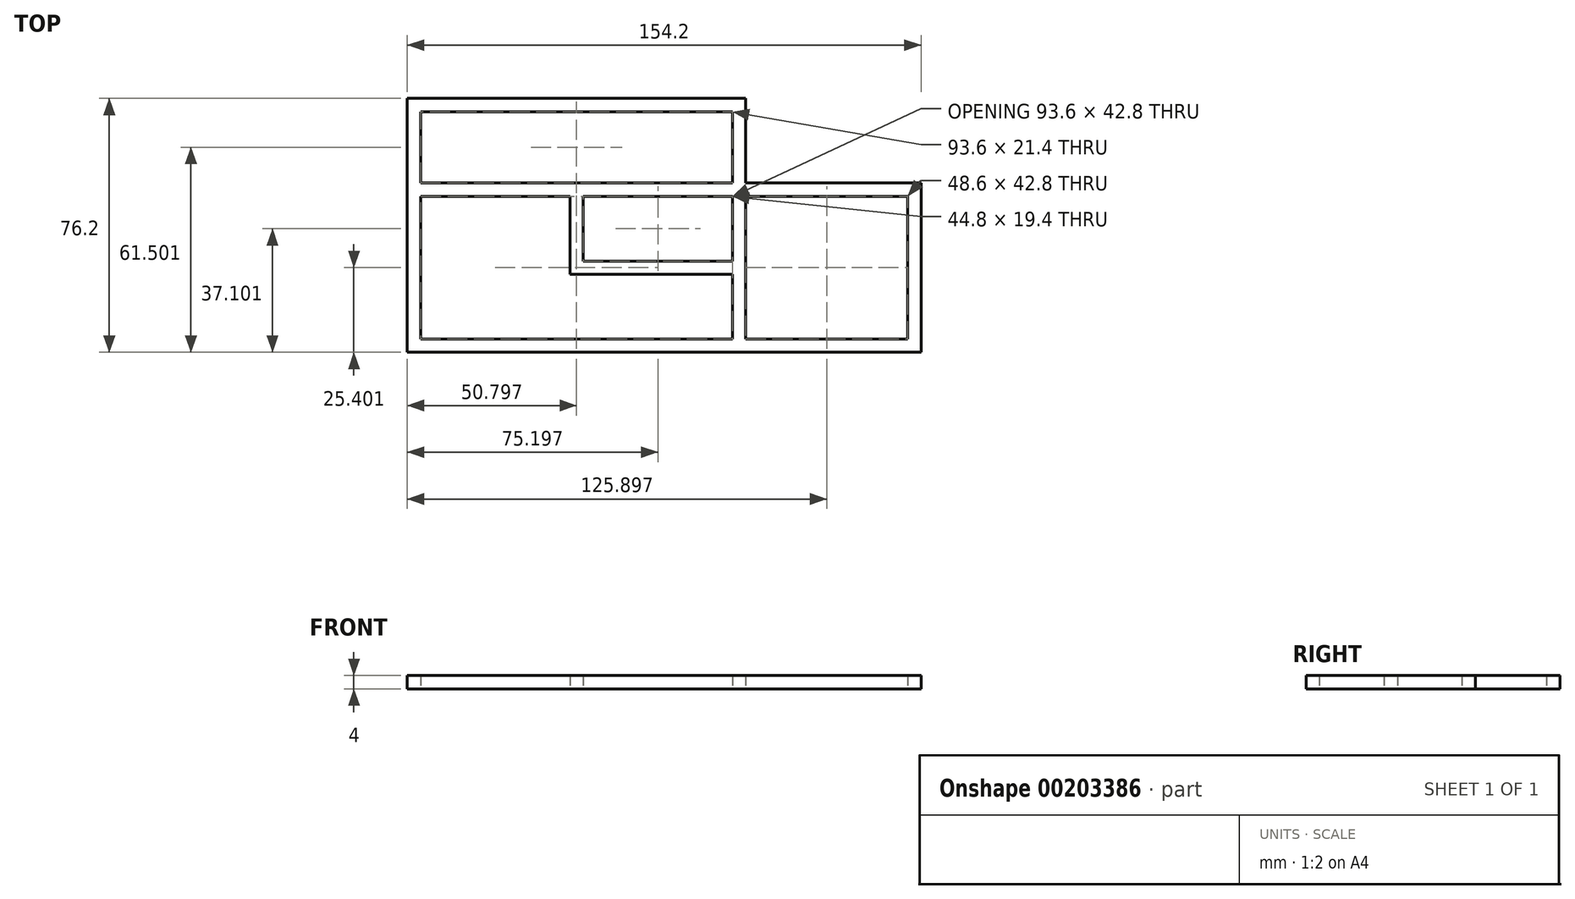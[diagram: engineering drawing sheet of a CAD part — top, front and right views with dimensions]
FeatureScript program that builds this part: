
annotation { "Feature Type Name" : "Feature", "Feature Type Description" : "" }
export const myFeature = defineFeature(function(context is Context, id is Id, definition is map)
    precondition{}
    {
        {
            var Q0;
            Q0=qCreatedBy(makeId("Top.planeOp"),FACE);
            var sketch = newSketch(context, id + "F0", { "sketchPlane" : qUnion([Q0])});
            skLineSegment(sketch, "E0", {"start": v(-122.43, 23.18) * mm, "end": v(-20.83, 23.18) * mm});
            skLineSegment(sketch, "E1", {"start": v(-20.83, 23.18) * mm, "end": v(-20.83, -2.22) * mm});
            skLineSegment(sketch, "E2", {"start": v(-20.83, -2.22) * mm, "end": v(31.77, -2.22) * mm});
            skLineSegment(sketch, "E3", {"start": v(31.77, -2.22) * mm, "end": v(31.77, -53.02) * mm});
            skLineSegment(sketch, "E4", {"start": v(31.77, -53.02) * mm, "end": v(-122.43, -53.02) * mm});
            skLineSegment(sketch, "E5", {"start": v(-122.43, -53.02) * mm, "end": v(-122.43, 23.18) * mm});
            skLineSegment(sketch, "E6", {"start": v(-118.43, 19.18) * mm, "end": v(-118.43, -49.02) * mm});
            skLineSegment(sketch, "E7", {"start": v(-118.43, -49.02) * mm, "end": v(27.77, -49.02) * mm});
            skLineSegment(sketch, "E8", {"start": v(27.77, -49.02) * mm, "end": v(27.77, -6.22) * mm});
            skLineSegment(sketch, "E9", {"start": v(27.77, -6.22) * mm, "end": v(-24.83, -6.22) * mm});
            skLineSegment(sketch, "E10", {"start": v(-24.83, -6.22) * mm, "end": v(-24.83, 19.18) * mm});
            skLineSegment(sketch, "E11", {"start": v(-24.83, 19.18) * mm, "end": v(-118.43, 19.18) * mm});
            skLineSegment(sketch, "E12", {"start": v(-24.83, -6.22) * mm, "end": v(-118.43, -6.22) * mm});
            skLineSegment(sketch, "E13", {"start": v(-20.83, -2.22) * mm, "end": v(-118.43, -2.22) * mm});
            skLineSegment(sketch, "E14", {"start": v(-24.83, -6.22) * mm, "end": v(-24.83, -49.02) * mm});
            skLineSegment(sketch, "E15", {"start": v(-20.83, -2.22) * mm, "end": v(-20.83, -49.02) * mm});
            skLineSegment(sketch, "E16.bottom", {"start": v(-73.63, 19.18) * mm, "end": v(-69.63, 19.18) * mm});
            skLineSegment(sketch, "E16.top", {"start": v(-73.63, -49.02) * mm, "end": v(-69.63, -49.02) * mm});
            skLineSegment(sketch, "E16.left", {"start": v(-73.63, 19.18) * mm, "end": v(-73.63, -49.02) * mm});
            skLineSegment(sketch, "E16.right", {"start": v(-69.63, 19.18) * mm, "end": v(-69.63, -49.02) * mm});
            skLineSegment(sketch, "E17.bottom", {"start": v(-118.43, -25.62) * mm, "end": v(27.77, -25.62) * mm});
            skLineSegment(sketch, "E17.top", {"start": v(-118.43, -29.62) * mm, "end": v(27.77, -29.62) * mm});
            skLineSegment(sketch, "E17.left", {"start": v(-118.43, -25.62) * mm, "end": v(-118.43, -29.62) * mm});
            skLineSegment(sketch, "E17.right", {"start": v(27.77, -25.62) * mm, "end": v(27.77, -29.62) * mm});
            skSolve(sketch);
        }
        {
            var Q0;
            Q0=makeQuery(id+"F0.imprint","IMPRINT",FACE,{"disambiguationData":[TD([[makeQuery(id+"F0.imprint","IMPRINT",EDGE,{"derivedFrom":sQuery(id+"F0.wireOp",EDGE,"E0")}),-1.0]])]});
            var Q1;
            {var subQ5=sQuery(id+"F0.wireOp",EDGE,"E16.bottom");Q1=makeQuery(id+"F0.imprint","IMPRINT",FACE,{"disambiguationData":[TD([[makeQuery(id+"F0.imprint","IMPRINT",EDGE,{"derivedFrom":subQ5}),-1.0]])]});}
            var Q2;
            {var subQ0=sQuery(id+"F0.wireOp",EDGE,"E16.right");var subQ1=sQuery(id+"F0.wireOp",EDGE,"E12");var subQ2=makeQuery(id+"F0.imprint","INTERSECT",VERTEX,{"derivedFrom":[subQ1,subQ0]});Q2=makeQuery(id+"F0.imprint","IMPRINT",FACE,{"disambiguationData":[TD([[makeQuery(id+"F0.imprint","IMPRINT",EDGE,{"disambiguationData":[TD([[subQ2,-1.0]])],"derivedFrom":subQ1}),-1.0]])]});}
            var Q3;
            {var subQ0=sQuery(id+"F0.wireOp",EDGE,"E12");var subQ1=sQuery(id+"F0.wireOp",EDGE,"E6");var subQ2=makeQuery(id+"F0.imprint","INTERSECT",VERTEX,{"derivedFrom":[subQ1,subQ0]});Q3=makeQuery(id+"F0.imprint","IMPRINT",FACE,{"disambiguationData":[TD([[makeQuery(id+"F0.imprint","IMPRINT",EDGE,{"disambiguationData":[TD([[subQ2,1.0]])],"derivedFrom":subQ1}),1.0]])]});}
            var Q4;
            {var subQ0=sQuery(id+"F0.wireOp",EDGE,"E16.right");var subQ1=sQuery(id+"F0.wireOp",EDGE,"E12");var subQ2=makeQuery(id+"F0.imprint","INTERSECT",VERTEX,{"derivedFrom":[subQ1,subQ0]});Q4=makeQuery(id+"F0.imprint","IMPRINT",FACE,{"disambiguationData":[TD([[makeQuery(id+"F0.imprint","IMPRINT",EDGE,{"disambiguationData":[TD([[subQ2,-1.0]])],"derivedFrom":subQ1}),1.0]])]});}
            var Q5;
            {var subQ0=sQuery(id+"F0.wireOp",EDGE,"E17.bottom");var subQ1=sQuery(id+"F0.wireOp",EDGE,"E16.left");var subQ2=makeQuery(id+"F0.imprint","INTERSECT",VERTEX,{"derivedFrom":[subQ1,subQ0]});Q5=makeQuery(id+"F0.imprint","IMPRINT",FACE,{"disambiguationData":[TD([[makeQuery(id+"F0.imprint","IMPRINT",EDGE,{"disambiguationData":[TD([[subQ2,-1.0]])],"derivedFrom":subQ1}),1.0]])]});}
            var Q6;
            {var subQ5=sQuery(id+"F0.wireOp",EDGE,"E17.left");Q6=makeQuery(id+"F0.imprint","IMPRINT",FACE,{"disambiguationData":[TD([[makeQuery(id+"F0.imprint","IMPRINT",EDGE,{"derivedFrom":subQ5}),1.0]])]});}
            var Q7;
            {var subQ0=sQuery(id+"F0.wireOp",EDGE,"E16.top");Q7=makeQuery(id+"F0.imprint","IMPRINT",FACE,{"disambiguationData":[TD([[makeQuery(id+"F0.imprint","IMPRINT",EDGE,{"derivedFrom":subQ0}),1.0]])]});}
            var Q8;
            {var subQ1=sQuery(id+"F0.wireOp",EDGE,"E10");var subQ3=sQuery(id+"F0.wireOp",EDGE,"E13");var subQ4=makeQuery(id+"F0.imprint","INTERSECT",VERTEX,{"derivedFrom":[subQ1,subQ3]});Q8=makeQuery(id+"F0.imprint","IMPRINT",FACE,{"disambiguationData":[TD([[makeQuery(id+"F0.imprint","IMPRINT",EDGE,{"disambiguationData":[TD([[subQ4,-1.0]])],"derivedFrom":subQ3}),1.0]])]});}
            var Q9;
            {var subQ1=sQuery(id+"F0.wireOp",EDGE,"E9");var subQ3=sQuery(id+"F0.wireOp",EDGE,"E15");var subQ4=makeQuery(id+"F0.imprint","INTERSECT",VERTEX,{"derivedFrom":[subQ1,subQ3]});Q9=makeQuery(id+"F0.imprint","IMPRINT",FACE,{"disambiguationData":[TD([[makeQuery(id+"F0.imprint","IMPRINT",EDGE,{"disambiguationData":[TD([[subQ4,-1.0]])],"derivedFrom":subQ1}),-1.0]])]});}
            var Q10;
            {var subQ1=sQuery(id+"F0.wireOp",EDGE,"E9");var subQ3=sQuery(id+"F0.wireOp",EDGE,"E15");var subQ4=makeQuery(id+"F0.imprint","INTERSECT",VERTEX,{"derivedFrom":[subQ1,subQ3]});Q10=makeQuery(id+"F0.imprint","IMPRINT",FACE,{"disambiguationData":[TD([[makeQuery(id+"F0.imprint","IMPRINT",EDGE,{"disambiguationData":[TD([[subQ4,-1.0]])],"derivedFrom":subQ3}),-1.0]])]});}
            var Q11;
            {var subQ0=sQuery(id+"F0.wireOp",EDGE,"E17.bottom");var subQ1=sQuery(id+"F0.wireOp",EDGE,"E14");var subQ2=makeQuery(id+"F0.imprint","INTERSECT",VERTEX,{"derivedFrom":[subQ1,subQ0]});Q11=makeQuery(id+"F0.imprint","IMPRINT",FACE,{"disambiguationData":[TD([[makeQuery(id+"F0.imprint","IMPRINT",EDGE,{"disambiguationData":[TD([[subQ2,-1.0]])],"derivedFrom":subQ1}),-1.0]])]});}
            var Q12;
            {var subQ0=sQuery(id+"F0.wireOp",EDGE,"E17.bottom");var subQ1=sQuery(id+"F0.wireOp",EDGE,"E14");var subQ2=makeQuery(id+"F0.imprint","INTERSECT",VERTEX,{"derivedFrom":[subQ1,subQ0]});Q12=makeQuery(id+"F0.imprint","IMPRINT",FACE,{"disambiguationData":[TD([[makeQuery(id+"F0.imprint","IMPRINT",EDGE,{"disambiguationData":[TD([[subQ2,-1.0]])],"derivedFrom":subQ1}),1.0]])]});}
            var Q13;
            {var subQ0=sQuery(id+"F0.wireOp",EDGE,"E14");var subQ1=sQuery(id+"F0.wireOp",EDGE,"E7");var subQ2=makeQuery(id+"F0.imprint","INTERSECT",VERTEX,{"derivedFrom":[subQ1,subQ0]});Q13=makeQuery(id+"F0.imprint","IMPRINT",FACE,{"disambiguationData":[TD([[makeQuery(id+"F0.imprint","IMPRINT",EDGE,{"disambiguationData":[TD([[subQ2,-1.0]])],"derivedFrom":subQ1}),1.0]])]});}
            var Q14;
            {var subQ5=sQuery(id+"F0.wireOp",EDGE,"E17.right");Q14=makeQuery(id+"F0.imprint","IMPRINT",FACE,{"disambiguationData":[TD([[makeQuery(id+"F0.imprint","IMPRINT",EDGE,{"derivedFrom":subQ5}),-1.0]])]});}
            extrude(context, id + "F1", {"entities" : qUnion([Q0, Q1, Q2, Q3, Q4, Q5, Q6, Q7, Q8, Q9, Q10, Q11, Q12, Q13, Q14]), "depth" : 4 * mm});
        }
    });
